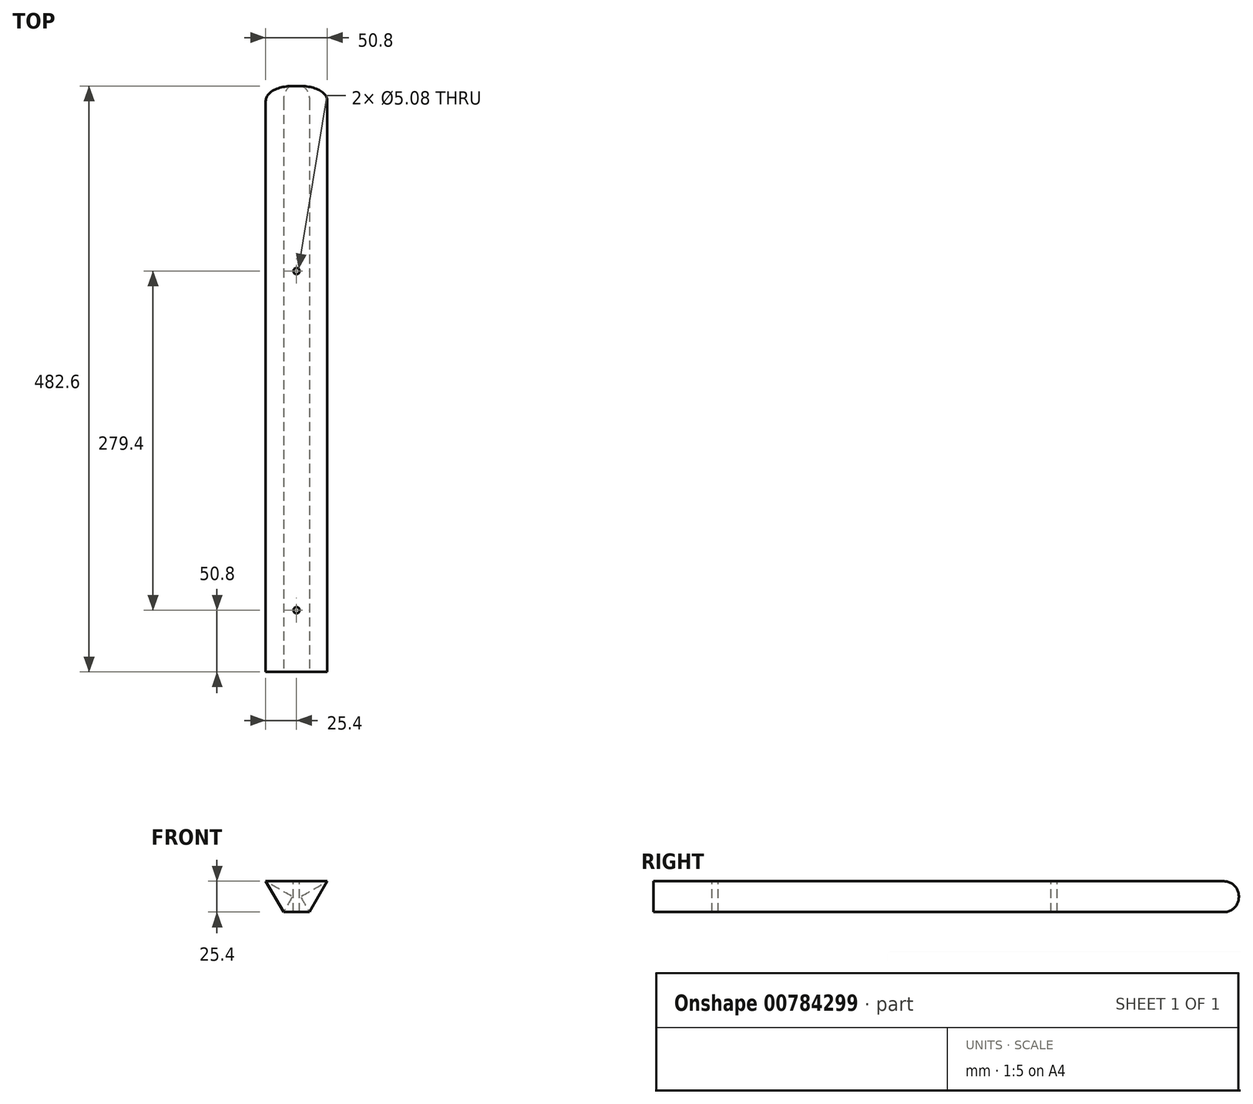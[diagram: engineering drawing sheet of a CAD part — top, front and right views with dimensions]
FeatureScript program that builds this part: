
annotation { "Feature Type Name" : "Feature", "Feature Type Description" : "" }
export const myFeature = defineFeature(function(context is Context, id is Id, definition is map)
    precondition{}
    {
        {
            var Q0;
            Q0=qCreatedBy(makeId("Front.planeOp"),FACE);
            var sketch = newSketch(context, id + "F0", { "sketchPlane" : qUnion([Q0])});
            skLineSegment(sketch, "E0.bottom", {"start": v(-25.4, 12.7) * mm, "end": v(25.4, 12.7) * mm});
            skLineSegment(sketch, "E0.top", {"start": v(-10.74, -12.7) * mm, "end": v(10.74, -12.7) * mm});
            skPoint(sketch, "E0.middle", {"position": v(0, 0) * mm});
            skLineSegment(sketch, "E1", {"start": v(-25.4, 12.7) * mm, "end": v(-10.74, -12.7) * mm});
            skLineSegment(sketch, "E2", {"start": v(25.4, 12.7) * mm, "end": v(10.74, -12.7) * mm});
            skPoint(sketch, "E0.left.end.orphan", {"position": v(-25.4, -12.7) * mm});
            skPoint(sketch, "E3.orphan", {"position": v(25.4, -12.7) * mm});
            skSolve(sketch);
        }
        {
            var Q0;
            Q0 = qSketchRegion(id + "F0", true);
            extrude(context, id + "F1", {"entities" : qUnion([Q0]), "oppositeDirection" : true, "depth" : 482.6 * mm, "offsetDistance" : 25.4 * mm});
        }
        {
            var Q0;
            Q0=makeQuery(id+"F1.opExtrude","CAP_EDGE",EDGE,{"disambiguationData":[OSD([sQuery(id+"F0.wireOp",EDGE,"E0.bottom")])],"isStart":false});
            var Q1;
            Q1=makeQuery(id+"F1.opExtrude","CAP_EDGE",EDGE,{"disambiguationData":[OSD([sQuery(id+"F0.wireOp",EDGE,"E2")])],"isStart":false});
            var Q2;
            Q2=makeQuery(id+"F1.opExtrude","CAP_EDGE",EDGE,{"disambiguationData":[OSD([sQuery(id+"F0.wireOp",EDGE,"E0.top")])],"isStart":false});
            var Q3;
            Q3=makeQuery(id+"F1.opExtrude","CAP_EDGE",EDGE,{"disambiguationData":[OSD([sQuery(id+"F0.wireOp",EDGE,"E1")])],"isStart":false});
            fillet(context, id + "F2", {"entities" : qUnion([Q0, Q1, Q2, Q3]), "radius" : 12.26 * mm, "tangentPropagation" : true, "allowEdgeOverflow" : false});
        }
        {
            var Q0;
            Q0=makeQuery(id+"F1.opExtrude","SWEPT_FACE",FACE,{"disambiguationData":[OSD([sQuery(id+"F0.wireOp",EDGE,"E0.bottom")])]});
            cPlane(context, id + "F3", {"entities" : qUnion([Q0]), "cplaneType" : CPlaneType.OFFSET, "offset" : 0 * mm, "width" : 152.4 * mm, "height" : 152.4 * mm});
        }
        {
            var Q0;
            Q0=qCreatedBy(id+"F3.planeOp",FACE);
            var sketch = newSketch(context, id + "F4", { "sketchPlane" : qUnion([Q0])});
            skLineSegment(sketch, "E4.bottom", {"start": v(25.4, 0) * mm, "end": v(-25.4, 0) * mm});
            skLineSegment(sketch, "E4.top", {"start": v(25.4, 482.6) * mm, "end": v(-25.4, 482.6) * mm});
            skLineSegment(sketch, "E4.left", {"start": v(25.4, 0) * mm, "end": v(25.4, 482.6) * mm});
            skLineSegment(sketch, "E4.right", {"start": v(-25.4, 0) * mm, "end": v(-25.4, 482.6) * mm});
            skLineSegment(sketch, "E5", {"start": v(-25.4, 330.2) * mm, "end": v(25.4, 330.2) * mm});
            skCircle(sketch, "E6", {"center": v(0, 330.2) * mm, "radius": 12.7 * mm});
            skLineSegment(sketch, "E7", {"start": v(25.4, 50.8) * mm, "end": v(-25.4, 50.8) * mm});
            skCircle(sketch, "E8", {"center": v(0, 50.8) * mm, "radius": 12.7 * mm});
            skSolve(sketch);
        }
        {
            var Q0;
            Q0=sQuery(id+"F4.wireOp",VERTEX,"E6.center");
            var Q1;
            Q1=sQuery(id+"F4.wireOp",VERTEX,"E8.center");
            var Q2;
            Q2=makeQuery(id+"F1.opExtrude","SWEPT_BODY",BODY,{"disambiguationData":[OSD([sQuery(id+"F0.wireOp",EDGE,"E0.bottom"),sQuery(id+"F0.wireOp",EDGE,"E0.top"),sQuery(id+"F0.wireOp",EDGE,"E1"),sQuery(id+"F0.wireOp",EDGE,"E2")])]});
            hole(context, id + "F5", {"style" : HoleStyle.SIMPLE, "endStyle" : HoleEndStyle.THROUGH, "holeDiameter" : 5.08 * mm, "majorDiameter" : 6.35 * mm, "isTappedThrough" : true, "tappedDepth" : 12.7 * mm, "tapClearance" : 3, "locations" : qUnion([Q0, Q1]), "scope" : qUnion([Q2])});
        }
    });
